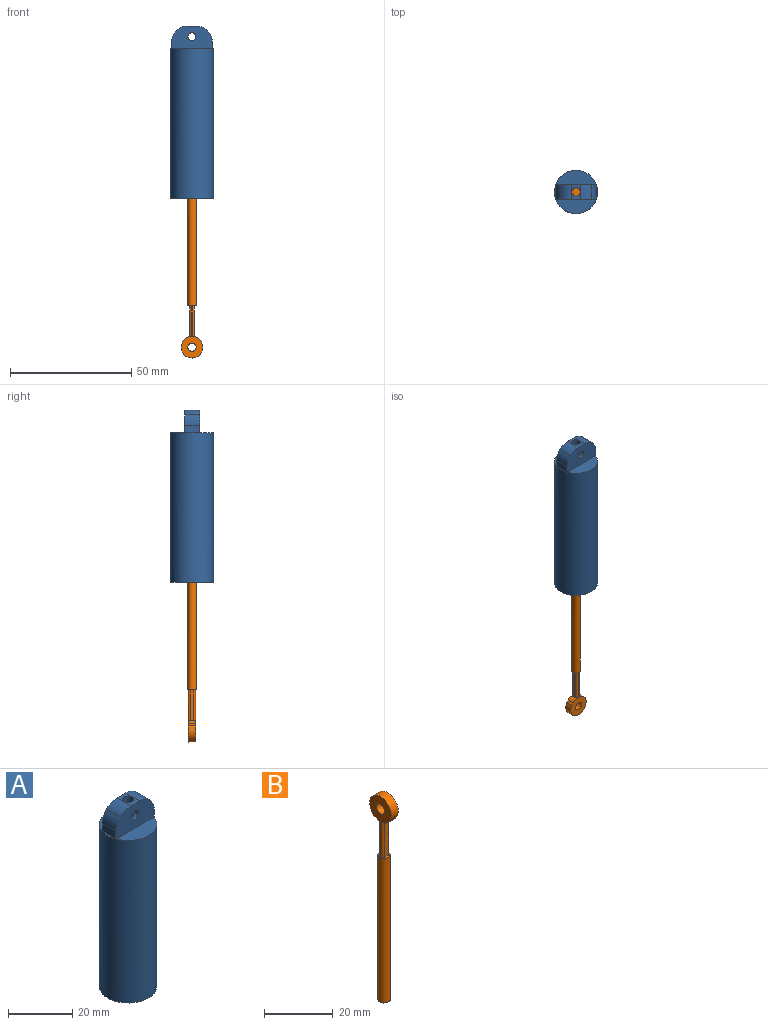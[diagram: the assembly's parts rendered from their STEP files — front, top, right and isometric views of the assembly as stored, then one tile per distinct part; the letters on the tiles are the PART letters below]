
ASSEMBLY  parts=2 mates=1
PART A: 19 faces, bbox 17.8x17.8x71.1 mm
  f0: cylinder r=1.78mm len=71.12mm, axis (0,0,-1), area 774.2mm2, adj f5,f10,f17,f18
  f1: plane 17.28x12.03mm, normal (0,0,1), area 75.3mm2, adj f3,f7,f8
  f2: plane 5.87x0.5mm, normal (0,0,1), area 2mm2, adj f3,f9
  f3: cylinder r=8.89mm len=65.64mm, axis (0,0,-1), area 3448.4mm2, adj f1,f2,f4,f5,f6,f9,f14
  f4: plane 16.64x5.75mm, normal (0,0,1), area 69.5mm2, adj f3,f6
  f5: plane 17.78x17.78mm, normal (0,0,-1), area 238.4mm2, adj f0,f3
  f6: plane 16.64x9.4mm, normal (0,-1,0), area 130.2mm2, adj f3,f4,f7,f10,f11,f12,f13,f14
  f7: plane 6.07x2.96mm, normal (1,0,0), area 18mm2, adj f1,f6,f8,f13
  f8: plane 16.71x9.4mm, normal (0,1,0), area 130.5mm2, adj f1,f7,f9,f10,f11,f12,f13,f14
  f9: plane 5.87x2.96mm, normal (-1,0,0), area 17.4mm2, adj f2,f3,f8,f14
  f10: plane 6.07x3.83mm, normal (0,0,1), area 13.3mm2, adj f0,f6,f8,f15,f16
  f11: plane 6.07x0.09mm, normal (-0.71,0,0.71), area 0.8mm2, adj f6,f8,f14,f15
  f12: plane 6.07x0.09mm, normal (0.71,0,0.71), area 0.8mm2, adj f6,f8,f13,f16
  f13: cylinder r=6.35mm len=6.07mm, axis (0,1,0), area 30.3mm2, adj f6,f7,f8,f12
  f14: cylinder r=6.35mm len=6.07mm, axis (0,-1,0), area 30.2mm2, adj f3,f6,f8,f9,f11
  f15: cylinder r=6.35mm len=6.07mm, axis (0,-1,0), area 30.3mm2, adj f6,f8,f10,f11
  f16: cylinder r=6.35mm len=6.07mm, axis (0,-1,0), area 30.3mm2, adj f6,f8,f10,f12
  f17: cylinder r=1.65mm len=3.3mm, axis (0,-1,0), area 17.1mm2, adj f0,f8
  f18: cylinder r=1.65mm len=3.3mm, axis (0,-1,0), area 19.2mm2, adj f0,f6
PART B: 18 faces, bbox 3.6x8.9x73.1 mm
  f0: plane 3.56x3.56mm, normal (0,0,1), area 4.5mm2, adj f1,f3,f4,f5,f6,f14,f15,f16
  f1: cylinder r=1.78mm len=51.56mm, axis (0,0,-1), area 576mm2, adj f0,f2
  f2: plane 3.56x3.56mm, normal (0,0,-1), area 9.9mm2, adj f1
  f3: plane 12.7x0.5mm, normal (-1,0,0), area 6.3mm2, adj f0,f13,f14,f17
  f4: plane 12.7x1.4mm, normal (0,-1,0), area 17.8mm2, adj f0,f12,f14,f15
  f5: plane 21.5x8.92mm, normal (1,0,0), area 59.5mm2, adj f0,f7,f8,f9,f10,f11,f12,f15
  f6: plane 12.7x1.4mm, normal (0,1,0), area 17.8mm2, adj f0,f7,f16,f17
  f7: cylinder r=4.46mm len=2.92mm, axis (1,0,0), area 7.7mm2, adj f5,f6,f8,f13,f16,f17
  f8: extruded ~2.92x0.99mm, area 3.7mm2, adj f5,f7,f9,f13
  f9: cylinder r=4.46mm len=8.92mm, axis (1,0,0), area 54.3mm2, adj f5,f8,f10,f13
  f10: extruded ~2.92x0.99mm, area 3.7mm2, adj f5,f9,f12,f13
  f11: cylinder r=1.7mm len=3.41mm, axis (1,0,0), area 31.3mm2, adj f5,f13
  f12: cylinder r=4.46mm len=2.92mm, axis (1,0,0), area 7.7mm2, adj f4,f5,f10,f13,f14,f15
  f13: plane 8.92x8.91mm, normal (-1,0,0), area 53.2mm2, adj f3,f7,f8,f9,f10,f11,f12,f14
  f14: cylinder r=0.76mm len=12.7mm, axis (0,0,-1), area 15.1mm2, adj f0,f3,f4,f12,f13
  f15: cylinder r=0.76mm len=12.7mm, axis (0,0,-1), area 15.1mm2, adj f0,f4,f5,f12
  f16: cylinder r=0.76mm len=12.7mm, axis (0,0,-1), area 15.1mm2, adj f0,f5,f6,f7
  f17: cylinder r=0.76mm len=12.7mm, axis (0,0,-1), area 15.1mm2, adj f0,f3,f6,f7,f13
PLACE A t=(8.24,-16.92,82.22)mm
PLACE B rot(axis=(0.71,-0.71,0),180deg) t=(-15.1,0.54,89.38)mm
MATE slider B.f1 <-> A.f0  axis (0,0,1) through (-15.1,0.54,63.6)mm
